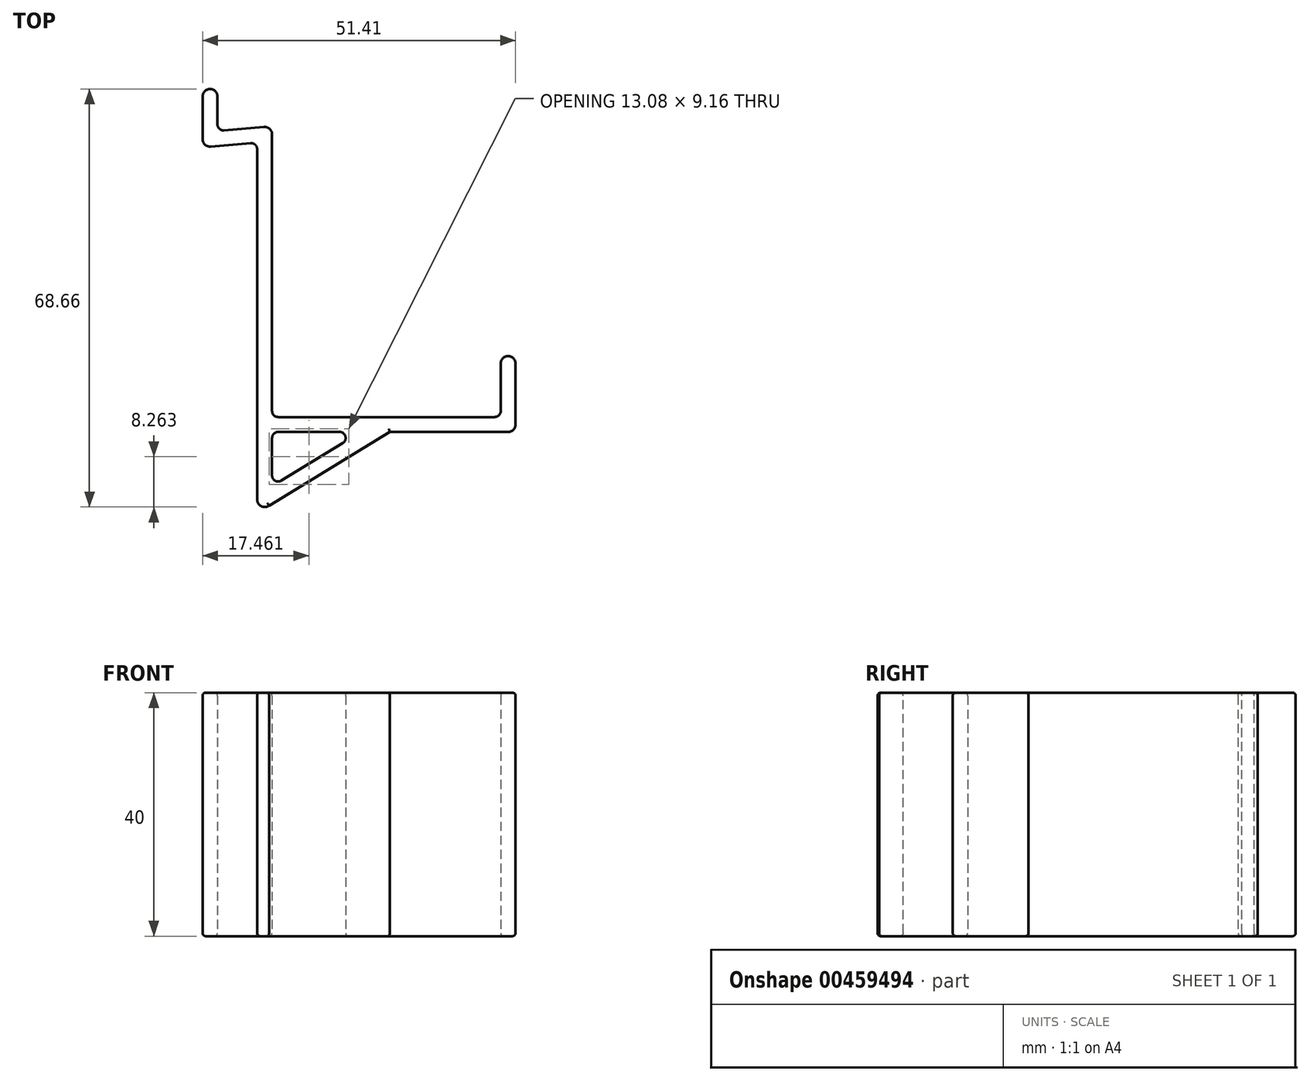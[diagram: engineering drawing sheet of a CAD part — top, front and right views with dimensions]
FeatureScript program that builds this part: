
annotation { "Feature Type Name" : "Feature", "Feature Type Description" : "" }
export const myFeature = defineFeature(function(context is Context, id is Id, definition is map)
    precondition{}
    {
        {
            var Q0;
            Q0=qCreatedBy(makeId("Top.planeOp"),FACE);
            var sketch = newSketch(context, id + "F0", { "sketchPlane" : qUnion([Q0])});
            skLineSegment(sketch, "E0", {"start": v(-29.17, 23.59) * mm, "end": v(-29.17, 16.59) * mm});
            skLineSegment(sketch, "E1", {"start": v(-29.17, 16.59) * mm, "end": v(-20.2, 17.37) * mm});
            skLineSegment(sketch, "E2", {"start": v(-20.2, 17.37) * mm, "end": v(-20.2, -42.63) * mm});
            skArc(sketch, "E3.0.startCap", {"start": v(-30.4, 23.59) * mm, "mid": v(-29.17, 24.81) * mm, "end": v(-27.95, 23.59) * mm});
            skArc(sketch, "E3.0.endCap", {"start": v(-27.95, 16.59) * mm, "mid": v(-29.17, 15.36) * mm, "end": v(-30.4, 16.59) * mm});
            skLineSegment(sketch, "E3.0.left", {"start": v(-27.95, 23.59) * mm, "end": v(-27.95, 16.59) * mm});
            skLineSegment(sketch, "E3.0.right", {"start": v(-30.4, 23.59) * mm, "end": v(-30.4, 16.59) * mm});
            skArc(sketch, "E3.1.startCap", {"start": v(-29.06, 15.37) * mm, "mid": v(-30.4, 16.48) * mm, "end": v(-29.28, 17.8) * mm});
            skArc(sketch, "E3.1.endCap", {"start": v(-20.31, 18.6) * mm, "mid": v(-18.99, 17.48) * mm, "end": v(-20.1, 16.15) * mm});
            skLineSegment(sketch, "E3.1.left", {"start": v(-29.28, 17.8) * mm, "end": v(-20.31, 18.6) * mm});
            skLineSegment(sketch, "E3.1.right", {"start": v(-29.06, 15.37) * mm, "end": v(-20.1, 16.15) * mm});
            skArc(sketch, "E3.2.startCap", {"start": v(-21.43, 17.37) * mm, "mid": v(-20.2, 18.6) * mm, "end": v(-18.98, 17.37) * mm});
            skArc(sketch, "E3.2.endCap", {"start": v(-18.98, -42.63) * mm, "mid": v(-20.2, -43.85) * mm, "end": v(-21.43, -42.63) * mm});
            skLineSegment(sketch, "E3.2.left", {"start": v(-18.98, 17.37) * mm, "end": v(-18.98, -42.63) * mm});
            skLineSegment(sketch, "E3.2.right", {"start": v(-21.43, 17.37) * mm, "end": v(-21.43, -42.63) * mm});
            skLineSegment(sketch, "E4", {"start": v(-20.2, -30.29) * mm, "end": v(19.8, -30.29) * mm});
            skLineSegment(sketch, "E5", {"start": v(19.8, -30.29) * mm, "end": v(19.8, -20.29) * mm});
            skArc(sketch, "E6.0.endCap", {"start": v(19.8, -29.07) * mm, "mid": v(21.01, -30.29) * mm, "end": v(19.8, -31.5) * mm});
            skLineSegment(sketch, "E6.0.left", {"start": v(-20.2, -29.07) * mm, "end": v(19.8, -29.07) * mm});
            skLineSegment(sketch, "E6.0.right", {"start": v(-20.2, -31.5) * mm, "end": v(19.8, -31.5) * mm});
            skArc(sketch, "E6.1.startCap", {"start": v(21.01, -30.29) * mm, "mid": v(19.8, -31.5) * mm, "end": v(18.57, -30.29) * mm});
            skArc(sketch, "E6.1.endCap", {"start": v(18.57, -20.29) * mm, "mid": v(19.8, -19.07) * mm, "end": v(21.01, -20.29) * mm});
            skLineSegment(sketch, "E6.1.left", {"start": v(18.57, -30.29) * mm, "end": v(18.57, -20.29) * mm});
            skLineSegment(sketch, "E6.1.right", {"start": v(21.01, -30.29) * mm, "end": v(21.01, -20.29) * mm});
            skLineSegment(sketch, "E7", {"start": v(-20.2, -42.63) * mm, "end": v(0, -30.29) * mm});
            skArc(sketch, "E8.0.startCap", {"start": v(-19.57, -43.67) * mm, "mid": v(-21.25, -43.26) * mm, "end": v(-20.84, -41.58) * mm});
            skArc(sketch, "E8.0.endCap", {"start": v(-0.64, -29.25) * mm, "mid": v(1.04, -29.65) * mm, "end": v(0.64, -31.33) * mm});
            skLineSegment(sketch, "E8.0.left", {"start": v(-20.84, -41.58) * mm, "end": v(-0.64, -29.25) * mm});
            skLineSegment(sketch, "E8.0.right", {"start": v(-19.57, -43.67) * mm, "end": v(0.64, -31.33) * mm});
            skSolve(sketch);
        }
        {
            var Q0;
            Q0 = qSketchRegion(id + "F0", true);
            var Q1;
            {var subQ0=sQuery(id+"F0.wireOp",EDGE,"E4");var subQ1=sQuery(id+"F0.wireOp",EDGE,"E2");var subQ2=makeQuery(id+"F0.imprint","INTERSECT",VERTEX,{"derivedFrom":[subQ1,subQ0]});Q1=makeQuery(id+"F0.imprint","IMPRINT",FACE,{"disambiguationData":[TD([[makeQuery(id+"F0.imprint","IMPRINT",EDGE,{"disambiguationData":[TD([[subQ2,-1.0]])],"derivedFrom":subQ1}),1.0]])]});}
            var Q2;
            {var subQ0=sQuery(id+"F0.wireOp",EDGE,"E6.0.right");var subQ1=sQuery(id+"F0.wireOp",EDGE,"E2");var subQ2=makeQuery(id+"F0.imprint","INTERSECT",VERTEX,{"derivedFrom":[subQ1,subQ0]});Q2=makeQuery(id+"F0.imprint","IMPRINT",FACE,{"disambiguationData":[TD([[makeQuery(id+"F0.imprint","IMPRINT",EDGE,{"disambiguationData":[TD([[subQ2,-1.0]])],"derivedFrom":subQ1}),1.0]])]});}
            var Q3;
            {var subQ0=sQuery(id+"F0.wireOp",EDGE,"E7");var subQ1=sQuery(id+"F0.wireOp",EDGE,"E2");var subQ2=makeQuery(id+"F0.imprint","INTERSECT",VERTEX,{"derivedFrom":[subQ1,subQ0]});Q3=makeQuery(id+"F0.imprint","IMPRINT",FACE,{"disambiguationData":[TD([[makeQuery(id+"F0.imprint","IMPRINT",EDGE,{"disambiguationData":[TD([[subQ2,1.0]])],"derivedFrom":subQ1}),1.0]])]});}
            var Q4;
            {var subQ0=sQuery(id+"F0.wireOp",EDGE,"E8.0.left");var subQ1=sQuery(id+"F0.wireOp",EDGE,"E3.2.left");var subQ2=makeQuery(id+"F0.imprint","INTERSECT",VERTEX,{"derivedFrom":[subQ1,subQ0]});Q4=makeQuery(id+"F0.imprint","IMPRINT",FACE,{"disambiguationData":[TD([[makeQuery(id+"F0.imprint","IMPRINT",EDGE,{"disambiguationData":[TD([[subQ2,-1.0]])],"derivedFrom":subQ1}),1.0]])]});}
            var Q5;
            {var subQ0=sQuery(id+"F0.wireOp",EDGE,"E7");var subQ1=sQuery(id+"F0.wireOp",EDGE,"E4");var subQ2=makeQuery(id+"F0.imprint","INTERSECT",VERTEX,{"derivedFrom":[subQ1,subQ0]});Q5=makeQuery(id+"F0.imprint","IMPRINT",FACE,{"disambiguationData":[TD([[makeQuery(id+"F0.imprint","IMPRINT",EDGE,{"disambiguationData":[TD([[subQ2,1.0]])],"derivedFrom":subQ1}),-1.0]])]});}
            var Q6;
            {var subQ0=sQuery(id+"F0.wireOp",EDGE,"E4");var subQ1=sQuery(id+"F0.wireOp",EDGE,"E3.2.left");var subQ2=makeQuery(id+"F0.imprint","INTERSECT",VERTEX,{"derivedFrom":[subQ1,subQ0]});Q6=makeQuery(id+"F0.imprint","IMPRINT",FACE,{"disambiguationData":[TD([[makeQuery(id+"F0.imprint","IMPRINT",EDGE,{"disambiguationData":[TD([[subQ2,-1.0]])],"derivedFrom":subQ1}),1.0]])]});}
            extrude(context, id + "F1", {"entities" : qUnion([Q0, Q1, Q2, Q3, Q4, Q5, Q6]), "depth" : 40 * mm, "offsetDistance" : 25 * mm});
        }
        {
            var Q0;
            Q0=makeQuery(id+"F1.opExtrude","SWEPT_EDGE",EDGE,{"disambiguationData":[OSD([sQuery(id+"F0.wireOp",EDGE,"E6.0.left"),sQuery(id+"F0.wireOp",EDGE,"E6.1.left")])]});
            var Q1;
            Q1=makeQuery(id+"F1.opExtrude","SWEPT_EDGE",EDGE,{"disambiguationData":[OSD([sQuery(id+"F0.wireOp",EDGE,"E3.2.left"),sQuery(id+"F0.wireOp",EDGE,"E6.0.left")])]});
            var Q2;
            Q2=makeQuery(id+"F1.opExtrude","SWEPT_EDGE",EDGE,{"disambiguationData":[OSD([sQuery(id+"F0.wireOp",EDGE,"E6.0.right"),sQuery(id+"F0.wireOp",EDGE,"E8.0.left")])]});
            var Q3;
            Q3=makeQuery(id+"F1.opExtrude","SWEPT_EDGE",EDGE,{"disambiguationData":[OSD([sQuery(id+"F0.wireOp",EDGE,"E3.2.left"),sQuery(id+"F0.wireOp",EDGE,"E6.0.right")])]});
            var Q4;
            Q4=makeQuery(id+"F1.opExtrude","SWEPT_EDGE",EDGE,{"disambiguationData":[OSD([sQuery(id+"F0.wireOp",EDGE,"E3.2.left"),sQuery(id+"F0.wireOp",EDGE,"E8.0.left")])]});
            var Q5;
            Q5=makeQuery(id+"F1.opExtrude","SWEPT_EDGE",EDGE,{"disambiguationData":[OSD([sQuery(id+"F0.wireOp",EDGE,"E3.0.left"),sQuery(id+"F0.wireOp",EDGE,"E3.1.left")])]});
            var Q6;
            Q6=makeQuery(id+"F1.opExtrude","SWEPT_EDGE",EDGE,{"disambiguationData":[OSD([sQuery(id+"F0.wireOp",EDGE,"E3.1.right"),sQuery(id+"F0.wireOp",EDGE,"E3.2.right")])]});
            fillet(context, id + "F2", {"entities" : qUnion([Q0, Q1, Q2, Q3, Q4, Q5, Q6]), "radius" : 1 * mm, "tangentPropagation" : true, "allowEdgeOverflow" : false});
        }
        {
            var Q0;
            Q0=makeQuery(id+"F1.opExtrude","CAP_FACE",FACE,{"disambiguationData":[OSD([sQuery(id+"F0.wireOp",EDGE,"E3.0.startCap"),sQuery(id+"F0.wireOp",EDGE,"E3.0.left"),sQuery(id+"F0.wireOp",EDGE,"E3.0.right"),sQuery(id+"F0.wireOp",EDGE,"E3.1.startCap"),sQuery(id+"F0.wireOp",EDGE,"E3.1.left"),sQuery(id+"F0.wireOp",EDGE,"E3.1.right"),sQuery(id+"F0.wireOp",EDGE,"E3.2.startCap"),sQuery(id+"F0.wireOp",EDGE,"E3.2.endCap"),sQuery(id+"F0.wireOp",EDGE,"E3.2.left"),sQuery(id+"F0.wireOp",EDGE,"E3.2.right"),sQuery(id+"F0.wireOp",EDGE,"E6.0.left"),sQuery(id+"F0.wireOp",EDGE,"E6.0.right"),sQuery(id+"F0.wireOp",EDGE,"E6.1.startCap"),sQuery(id+"F0.wireOp",EDGE,"E6.1.endCap"),sQuery(id+"F0.wireOp",EDGE,"E6.1.left"),sQuery(id+"F0.wireOp",EDGE,"E6.1.right"),sQuery(id+"F0.wireOp",EDGE,"E8.0.left"),sQuery(id+"F0.wireOp",EDGE,"E8.0.right")])],"isStart":false});
            var Q1;
            Q1=makeQuery(id+"F1.opExtrude","CAP_FACE",FACE,{"disambiguationData":[OSD([sQuery(id+"F0.wireOp",EDGE,"E3.0.startCap"),sQuery(id+"F0.wireOp",EDGE,"E3.0.left"),sQuery(id+"F0.wireOp",EDGE,"E3.0.right"),sQuery(id+"F0.wireOp",EDGE,"E3.1.startCap"),sQuery(id+"F0.wireOp",EDGE,"E3.1.left"),sQuery(id+"F0.wireOp",EDGE,"E3.1.right"),sQuery(id+"F0.wireOp",EDGE,"E3.2.startCap"),sQuery(id+"F0.wireOp",EDGE,"E3.2.endCap"),sQuery(id+"F0.wireOp",EDGE,"E3.2.left"),sQuery(id+"F0.wireOp",EDGE,"E3.2.right"),sQuery(id+"F0.wireOp",EDGE,"E6.0.left"),sQuery(id+"F0.wireOp",EDGE,"E6.0.right"),sQuery(id+"F0.wireOp",EDGE,"E6.1.startCap"),sQuery(id+"F0.wireOp",EDGE,"E6.1.endCap"),sQuery(id+"F0.wireOp",EDGE,"E6.1.left"),sQuery(id+"F0.wireOp",EDGE,"E6.1.right"),sQuery(id+"F0.wireOp",EDGE,"E8.0.left"),sQuery(id+"F0.wireOp",EDGE,"E8.0.right")])],"isStart":true});
            fillet(context, id + "F3", {"entities" : qUnion([Q0, Q1]), "radius" : 0.5 * mm, "tangentPropagation" : true, "allowEdgeOverflow" : false});
        }
    });
